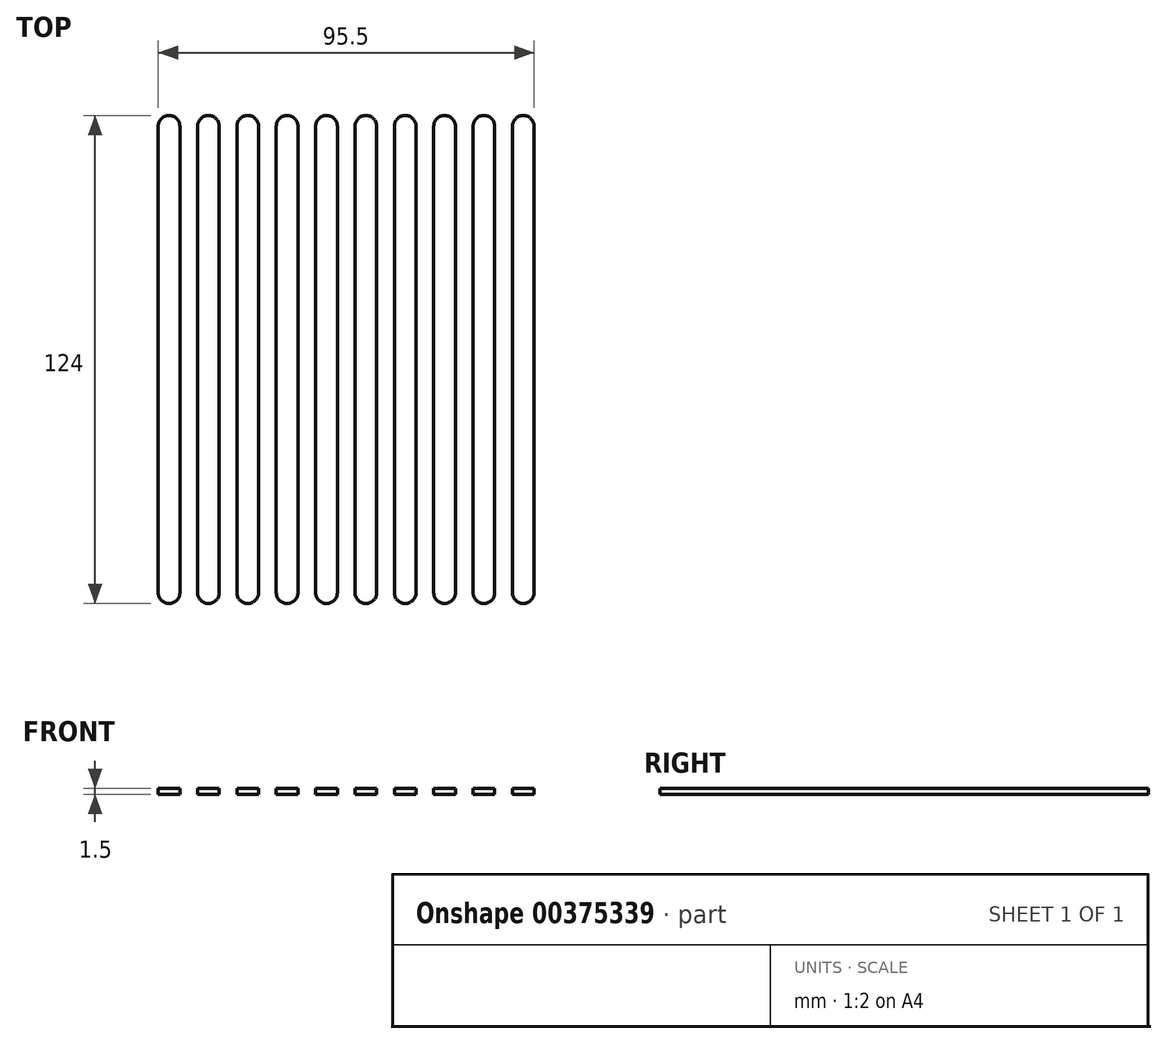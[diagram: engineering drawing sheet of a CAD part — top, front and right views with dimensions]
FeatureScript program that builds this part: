
annotation { "Feature Type Name" : "Feature", "Feature Type Description" : "" }
export const myFeature = defineFeature(function(context is Context, id is Id, definition is map)
    precondition{}
    {
        {
            var Q0;
            Q0=qCreatedBy(makeId("Top.planeOp"),FACE);
            var sketch = newSketch(context, id + "F0", { "sketchPlane" : qUnion([Q0])});
            skLineSegment(sketch, "E0.left", {"start": v(-2.75, -59.25) * mm, "end": v(-2.75, 59.25) * mm});
            skLineSegment(sketch, "E0.right", {"start": v(2.75, -59.25) * mm, "end": v(2.75, 59.25) * mm});
            skPoint(sketch, "E0.middle", {"position": v(0, 0) * mm});
            skArc(sketch, "E1", {"start": v(-2.75, 59.25) * mm, "mid": v(0, 62) * mm, "end": v(2.75, 59.25) * mm});
            skArc(sketch, "E2", {"start": v(2.75, -59.25) * mm, "mid": v(0, -62) * mm, "end": v(-2.75, -59.25) * mm});
            skLineSegment(sketch, "E3.1.0.0", {"start": v(12.75, -59.25) * mm, "end": v(12.75, 59.25) * mm});
            skPoint(sketch, "E3.1.0.1", {"position": v(10, 0) * mm});
            skLineSegment(sketch, "E3.1.0.2", {"start": v(7.25, -59.25) * mm, "end": v(7.25, 59.25) * mm});
            skArc(sketch, "E3.1.0.3", {"start": v(12.75, -59.25) * mm, "mid": v(10, -62) * mm, "end": v(7.25, -59.25) * mm});
            skArc(sketch, "E3.1.0.4", {"start": v(7.25, 59.25) * mm, "mid": v(10, 62) * mm, "end": v(12.75, 59.25) * mm});
            skLineSegment(sketch, "E3.2.0.0", {"start": v(22.75, -59.25) * mm, "end": v(22.75, 59.25) * mm});
            skPoint(sketch, "E3.2.0.1", {"position": v(20, 0) * mm});
            skLineSegment(sketch, "E3.2.0.2", {"start": v(17.25, -59.25) * mm, "end": v(17.25, 59.25) * mm});
            skArc(sketch, "E3.2.0.3", {"start": v(22.75, -59.25) * mm, "mid": v(20, -62) * mm, "end": v(17.25, -59.25) * mm});
            skArc(sketch, "E3.2.0.4", {"start": v(17.25, 59.25) * mm, "mid": v(20, 62) * mm, "end": v(22.75, 59.25) * mm});
            skLineSegment(sketch, "E3.3.0.0", {"start": v(32.75, -59.25) * mm, "end": v(32.75, 59.25) * mm});
            skPoint(sketch, "E3.3.0.1", {"position": v(30, 0) * mm});
            skLineSegment(sketch, "E3.3.0.2", {"start": v(27.25, -59.25) * mm, "end": v(27.25, 59.25) * mm});
            skArc(sketch, "E3.3.0.3", {"start": v(32.75, -59.25) * mm, "mid": v(30, -62) * mm, "end": v(27.25, -59.25) * mm});
            skArc(sketch, "E3.3.0.4", {"start": v(27.25, 59.25) * mm, "mid": v(30, 62) * mm, "end": v(32.75, 59.25) * mm});
            skLineSegment(sketch, "E3.4.0.0", {"start": v(42.75, -59.25) * mm, "end": v(42.75, 59.25) * mm});
            skPoint(sketch, "E3.4.0.1", {"position": v(40, 0) * mm});
            skLineSegment(sketch, "E3.4.0.2", {"start": v(37.25, -59.25) * mm, "end": v(37.25, 59.25) * mm});
            skArc(sketch, "E3.4.0.3", {"start": v(42.75, -59.25) * mm, "mid": v(40, -62) * mm, "end": v(37.25, -59.25) * mm});
            skArc(sketch, "E3.4.0.4", {"start": v(37.25, 59.25) * mm, "mid": v(40, 62) * mm, "end": v(42.75, 59.25) * mm});
            skLineSegment(sketch, "E3.5.0.0", {"start": v(52.75, -59.25) * mm, "end": v(52.75, 59.25) * mm});
            skPoint(sketch, "E3.5.0.1", {"position": v(50, 0) * mm});
            skLineSegment(sketch, "E3.5.0.2", {"start": v(47.25, -59.25) * mm, "end": v(47.25, 59.25) * mm});
            skArc(sketch, "E3.5.0.3", {"start": v(52.75, -59.25) * mm, "mid": v(50, -62) * mm, "end": v(47.25, -59.25) * mm});
            skArc(sketch, "E3.5.0.4", {"start": v(47.25, 59.25) * mm, "mid": v(50, 62) * mm, "end": v(52.75, 59.25) * mm});
            skLineSegment(sketch, "E3.6.0.0", {"start": v(62.75, -59.25) * mm, "end": v(62.75, 59.25) * mm});
            skPoint(sketch, "E3.6.0.1", {"position": v(60, 0) * mm});
            skLineSegment(sketch, "E3.6.0.2", {"start": v(57.25, -59.25) * mm, "end": v(57.25, 59.25) * mm});
            skArc(sketch, "E3.6.0.3", {"start": v(62.75, -59.25) * mm, "mid": v(60, -62) * mm, "end": v(57.25, -59.25) * mm});
            skArc(sketch, "E3.6.0.4", {"start": v(57.25, 59.25) * mm, "mid": v(60, 62) * mm, "end": v(62.75, 59.25) * mm});
            skLineSegment(sketch, "E3.7.0.0", {"start": v(72.75, -59.25) * mm, "end": v(72.75, 59.25) * mm});
            skPoint(sketch, "E3.7.0.1", {"position": v(70, 0) * mm});
            skLineSegment(sketch, "E3.7.0.2", {"start": v(67.25, -59.25) * mm, "end": v(67.25, 59.25) * mm});
            skArc(sketch, "E3.7.0.3", {"start": v(72.75, -59.25) * mm, "mid": v(70, -62) * mm, "end": v(67.25, -59.25) * mm});
            skArc(sketch, "E3.7.0.4", {"start": v(67.25, 59.25) * mm, "mid": v(70, 62) * mm, "end": v(72.75, 59.25) * mm});
            skLineSegment(sketch, "E3.8.0.0", {"start": v(82.75, -59.25) * mm, "end": v(82.75, 59.25) * mm});
            skPoint(sketch, "E3.8.0.1", {"position": v(80, 0) * mm});
            skLineSegment(sketch, "E3.8.0.2", {"start": v(77.25, -59.25) * mm, "end": v(77.25, 59.25) * mm});
            skArc(sketch, "E3.8.0.3", {"start": v(82.75, -59.25) * mm, "mid": v(80, -62) * mm, "end": v(77.25, -59.25) * mm});
            skArc(sketch, "E3.8.0.4", {"start": v(77.25, 59.25) * mm, "mid": v(80, 62) * mm, "end": v(82.75, 59.25) * mm});
            skLineSegment(sketch, "E3.9.0.0", {"start": v(92.75, -59.25) * mm, "end": v(92.75, 59.25) * mm});
            skPoint(sketch, "E3.9.0.1", {"position": v(90, 0) * mm});
            skLineSegment(sketch, "E3.9.0.2", {"start": v(87.25, -59.25) * mm, "end": v(87.25, 59.25) * mm});
            skArc(sketch, "E3.9.0.3", {"start": v(92.75, -59.25) * mm, "mid": v(90, -62) * mm, "end": v(87.25, -59.25) * mm});
            skArc(sketch, "E3.9.0.4", {"start": v(87.25, 59.25) * mm, "mid": v(90, 62) * mm, "end": v(92.75, 59.25) * mm});
            skLineSegment(sketch, "E3.direction1", {"start": v(-2.75, -59.25) * mm, "end": v(7.25, -59.25) * mm, "construction": true});
            skSolve(sketch);
        }
        {
            var Q0;
            Q0 = qSketchRegion(id + "F0", true);
            extrude(context, id + "F1", {"entities" : qUnion([Q0]), "depth" : 1.5 * mm});
        }
    });
